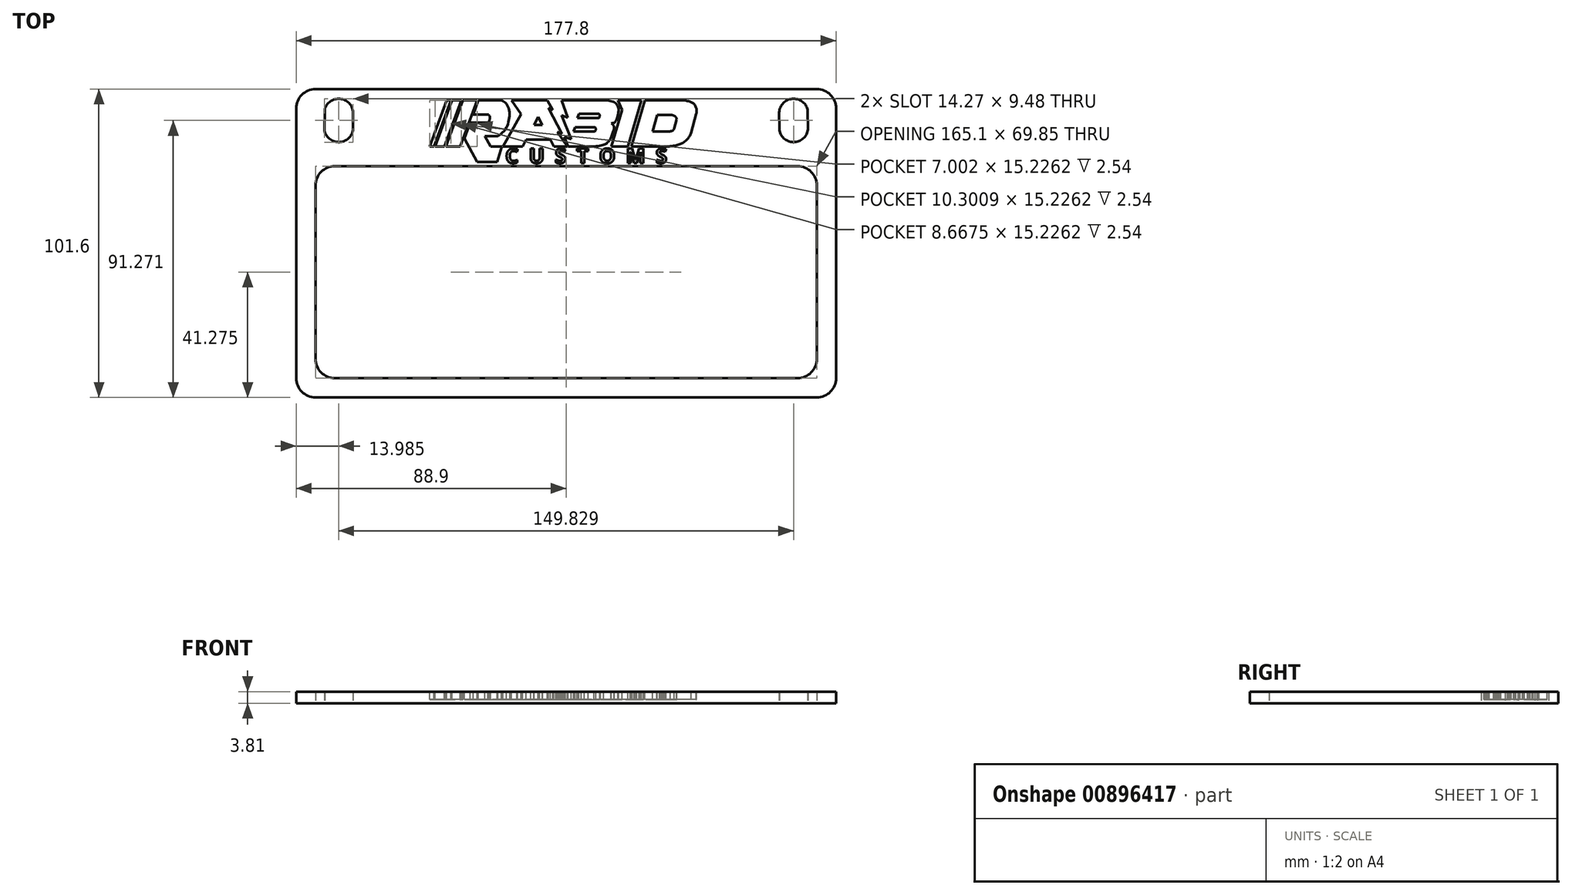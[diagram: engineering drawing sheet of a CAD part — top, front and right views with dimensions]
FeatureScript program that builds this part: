
annotation { "Feature Type Name" : "Feature", "Feature Type Description" : "" }
export const myFeature = defineFeature(function(context is Context, id is Id, definition is map)
    precondition{}
    {
        {
            var Q0;
            Q0=qCreatedBy(makeId("Top.planeOp"),FACE);
            var sketch = newSketch(context, id + "F0", { "sketchPlane" : qUnion([Q0])});
            skLineSegment(sketch, "E0.bottom", {"start": v(-82.55, 50.8) * mm, "end": v(82.55, 50.8) * mm});
            skLineSegment(sketch, "E0.top", {"start": v(-82.55, -50.8) * mm, "end": v(82.55, -50.8) * mm});
            skLineSegment(sketch, "E0.left", {"start": v(-88.9, 44.45) * mm, "end": v(-88.9, -44.45) * mm});
            skLineSegment(sketch, "E0.right", {"start": v(88.9, 44.45) * mm, "end": v(88.9, -44.45) * mm});
            skArc(sketch, "E1", {"start": v(-70.18, 43.14) * mm, "mid": v(-74.48, 47.6) * mm, "end": v(-79.55, 44.03) * mm});
            skArc(sketch, "E2", {"start": v(-79.65, 37.5) * mm, "mid": v(-74.85, 33.34) * mm, "end": v(-70.19, 37.65) * mm});
            skLineSegment(sketch, "E3", {"start": v(-79.55, 44.03) * mm, "end": v(-79.65, 37.5) * mm});
            skLineSegment(sketch, "E4", {"start": v(-70.18, 43.14) * mm, "end": v(-70.19, 37.65) * mm});
            skArc(sketch, "E5.filletArc", {"start": v(-82.55, 50.8) * mm, "mid": v(-87.04, 48.94) * mm, "end": v(-88.9, 44.45) * mm});
            skArc(sketch, "E6.filletArc", {"start": v(88.9, 44.45) * mm, "mid": v(87.04, 48.94) * mm, "end": v(82.55, 50.8) * mm});
            skArc(sketch, "E7.filletArc", {"start": v(82.55, -50.8) * mm, "mid": v(87.04, -48.94) * mm, "end": v(88.9, -44.45) * mm});
            skArc(sketch, "E8.filletArc", {"start": v(-88.9, -44.45) * mm, "mid": v(-87.04, -48.94) * mm, "end": v(-82.55, -50.8) * mm});
            skArc(sketch, "E9.MirrorCS", {"start": v(79.65, 37.5) * mm, "mid": v(74.85, 33.34) * mm, "end": v(70.19, 37.65) * mm});
            skLineSegment(sketch, "E10.MirrorCS", {"start": v(70.18, 43.14) * mm, "end": v(70.19, 37.65) * mm});
            skLineSegment(sketch, "E11.MirrorCS", {"start": v(79.55, 44.03) * mm, "end": v(79.65, 37.5) * mm});
            skArc(sketch, "E12.MirrorCS", {"start": v(70.18, 43.14) * mm, "mid": v(74.48, 47.6) * mm, "end": v(79.55, 44.03) * mm});
            skLineSegment(sketch, "E13.bottom", {"start": v(-76.2, 25.4) * mm, "end": v(76.2, 25.4) * mm});
            skLineSegment(sketch, "E13.top", {"start": v(-76.2, -44.45) * mm, "end": v(76.2, -44.45) * mm});
            skLineSegment(sketch, "E13.left", {"start": v(-82.55, 19.05) * mm, "end": v(-82.55, -38.1) * mm});
            skLineSegment(sketch, "E13.right", {"start": v(82.55, 19.05) * mm, "end": v(82.55, -38.1) * mm});
            skPoint(sketch, "E14.visualSharp", {"position": v(-82.55, 25.4) * mm});
            skArc(sketch, "E14.filletArc", {"start": v(-76.2, 25.4) * mm, "mid": v(-80.7, 23.54) * mm, "end": v(-82.55, 19.05) * mm});
            skPoint(sketch, "E15.visualSharp", {"position": v(82.55, 25.4) * mm});
            skArc(sketch, "E15.filletArc", {"start": v(82.55, 19.05) * mm, "mid": v(80.7, 23.54) * mm, "end": v(76.2, 25.4) * mm});
            skArc(sketch, "E16.filletArc", {"start": v(76.2, -44.45) * mm, "mid": v(80.7, -42.6) * mm, "end": v(82.55, -38.1) * mm});
            skArc(sketch, "E17.filletArc", {"start": v(-82.55, -38.1) * mm, "mid": v(-80.7, -42.6) * mm, "end": v(-76.2, -44.45) * mm});
            skSolve(sketch);
        }
        {
            var Q0;
            Q0=qSketchRegion(id+"F0",true);
            extrude(context, id + "F1", {"entities" : qUnion([Q0]), "depth" : 3.8 * mm, "offsetDistance" : 25.4 * mm});
        }
        {
            var Q0;
            Q0=makeQuery(id+"F1.opExtrude","CAP_FACE",FACE,{"disambiguationData":[OSD([sQuery(id+"F0.wireOp",EDGE,"E0.bottom"),sQuery(id+"F0.wireOp",EDGE,"E0.top"),sQuery(id+"F0.wireOp",EDGE,"E0.left"),sQuery(id+"F0.wireOp",EDGE,"E0.right"),sQuery(id+"F0.wireOp",EDGE,"5VO8HKmw-Esxs-SXYE-kqu2-tz63mqYEAXiB.bottom"),sQuery(id+"F0.wireOp",EDGE,"5VO8HKmw-Esxs-SXYE-kqu2-tz63mqYEAXiB.top"),sQuery(id+"F0.wireOp",EDGE,"5VO8HKmw-Esxs-SXYE-kqu2-tz63mqYEAXiB.left"),sQuery(id+"F0.wireOp",EDGE,"5VO8HKmw-Esxs-SXYE-kqu2-tz63mqYEAXiB.right"),sQuery(id+"F0.wireOp",EDGE,"ZtOqOz9P-OmnG-4Yyo-7eWy-nuA7kXPjKyah"),sQuery(id+"F0.wireOp",EDGE,"UhQ4hDFr-K4N2-AdQz-foQS-J1ex0guJvTy1"),sQuery(id+"F0.wireOp",EDGE,"N4FC6TI6-brI2-4AQh-qVUN-D9pu45Rl41Qv"),sQuery(id+"F0.wireOp",EDGE,"e420d8bd-9363-4734-b41a-eac7de9b64b6.trimOffspring"),sQuery(id+"F0.wireOp",EDGE,"E1"),sQuery(id+"F0.wireOp",EDGE,"E2"),sQuery(id+"F0.wireOp",EDGE,"E3"),sQuery(id+"F0.wireOp",EDGE,"E4"),sQuery(id+"F0.wireOp",EDGE,"388fb5a8-1ea3-4299-9213-5ed0e58871d10.MirrorCS"),sQuery(id+"F0.wireOp",EDGE,"388fb5a8-1ea3-4299-9213-5ed0e58871d11.MirrorCS"),sQuery(id+"F0.wireOp",EDGE,"388fb5a8-1ea3-4299-9213-5ed0e58871d12.MirrorCS"),sQuery(id+"F0.wireOp",EDGE,"388fb5a8-1ea3-4299-9213-5ed0e58871d13.MirrorCS"),sQuery(id+"F0.wireOp",EDGE,"388fb5a8-1ea3-4299-9213-5ed0e58871d14.MirrorCS"),sQuery(id+"F0.wireOp",EDGE,"388fb5a8-1ea3-4299-9213-5ed0e58871d15.MirrorCS"),sQuery(id+"F0.wireOp",EDGE,"388fb5a8-1ea3-4299-9213-5ed0e58871d16.MirrorCS"),sQuery(id+"F0.wireOp",EDGE,"e4d6ff06-b432-4113-9549-54836a44de97.trimOffspring"),sQuery(id+"F0.wireOp",EDGE,"343a162d-83e7-4e76-8459-f58917313968.filletArc"),sQuery(id+"F0.wireOp",EDGE,"E5.filletArc"),sQuery(id+"F0.wireOp",EDGE,"edaf4797-65b9-4c6f-aac9-da0511a8ee4a.filletArc"),sQuery(id+"F0.wireOp",EDGE,"E6.filletArc"),sQuery(id+"F0.wireOp",EDGE,"E7.filletArc"),sQuery(id+"F0.wireOp",EDGE,"03c890ec-8c51-4b18-90a4-88e655fb5f41.filletArc"),sQuery(id+"F0.wireOp",EDGE,"E8.filletArc"),sQuery(id+"F0.wireOp",EDGE,"408b96f7-1ce1-402e-bdab-98c03d327ea0.filletArc"),sQuery(id+"F0.wireOp",EDGE,"bjHKFNyx-CfJ5-pHdQ-Rjsu-5QMIBnfaj9aT"),sQuery(id+"F0.wireOp",EDGE,"hgvkDYSf-fWNe-M4NK-JL9C-AdpdUPqnzP5O"),sQuery(id+"F0.wireOp",EDGE,"OAJ1lY74-7GEf-kqh1-0pf5-185unJ51uZ2I"),sQuery(id+"F0.wireOp",EDGE,"7dc4cac3-4ac6-421c-a2db-e4ca0b0f0da1.trimOffspring"),sQuery(id+"F0.wireOp",EDGE,"83e6ecbc-63ed-4ffd-8922-6f6cd5348e8b.filletArc"),sQuery(id+"F0.wireOp",EDGE,"dcab3ff3-acb6-4ce3-92ec-6480daf3896c.filletArc"),sQuery(id+"F0.wireOp",EDGE,"7c8d1e97-1c9b-487b-8608-89f6ca3dd430.filletArc"),sQuery(id+"F0.wireOp",EDGE,"08c262f0-2f62-415d-b3e7-4e7392bdbc79.filletArc"),sQuery(id+"F0.wireOp",EDGE,"3e58efb5-ef9c-4a86-b57f-9bd11ee7677c.filletArc"),sQuery(id+"F0.wireOp",EDGE,"6554a4f9-b08c-4d9f-b403-859f83e8338b.filletArc"),sQuery(id+"F0.wireOp",EDGE,"495016f4-edd1-4ee5-bd80-bea4dd5b2a8f.filletArc"),sQuery(id+"F0.wireOp",EDGE,"2213c4b9-707a-4fd7-954b-32b890b75866.filletArc"),sQuery(id+"F0.wireOp",EDGE,"aa9dc5e7-3301-407e-8f38-505bf975b0c1.filletArc"),sQuery(id+"F0.wireOp",EDGE,"0aa655fa-f177-4ffa-a66b-476f03fc73f5.filletArc"),sQuery(id+"F0.wireOp",EDGE,"dca11e5c-dc25-4b1e-a035-025dcb39c10a.filletArc"),sQuery(id+"F0.wireOp",EDGE,"029dcba7-a7e0-4e25-897b-a3a4278317f0.filletArc")])],"isStart":false});
            var sketch = newSketch(context, id + "F2", { "sketchPlane" : qUnion([Q0])});
            skLineSegment(sketch, "E18", {"start": v(38.33, 47.13) * mm, "end": v(25.89, 47.13) * mm});
            skLineSegment(sketch, "E19", {"start": v(-44.97, 31.9) * mm, "end": v(-39.37, 47.13) * mm});
            skLineSegment(sketch, "E20", {"start": v(-34.91, 31.9) * mm, "end": v(-39.61, 31.9) * mm});
            skLineSegment(sketch, "E21", {"start": v(-37.97, 47.13) * mm, "end": v(-43.57, 31.9) * mm});
            skLineSegment(sketch, "E22", {"start": v(-43.14, 31.9) * mm, "end": v(-37.54, 47.13) * mm});
            skLineSegment(sketch, "E23", {"start": v(-34.47, 47.13) * mm, "end": v(-40.07, 31.9) * mm});
            skLineSegment(sketch, "E24", {"start": v(-39.61, 31.9) * mm, "end": v(-34, 47.13) * mm});
            skLineSegment(sketch, "E25", {"start": v(-29.31, 47.13) * mm, "end": v(-34.91, 31.9) * mm});
            skLineSegment(sketch, "E26", {"start": v(-30.63, 42.38) * mm, "end": v(-28.89, 47.13) * mm});
            skLineSegment(sketch, "E27", {"start": v(-30.63, 42.38) * mm, "end": v(-25.54, 42.38) * mm});
            skLineSegment(sketch, "E28", {"start": v(-25.82, 39.71) * mm, "end": v(-31.56, 39.71) * mm});
            skLineSegment(sketch, "E29", {"start": v(-31.56, 39.71) * mm, "end": v(-33.47, 34.53) * mm});
            skLineSegment(sketch, "E30", {"start": v(-33.47, 34.53) * mm, "end": v(-29.26, 26.81) * mm});
            skLineSegment(sketch, "E31", {"start": v(-29.26, 26.81) * mm, "end": v(-22.69, 26.81) * mm});
            skLineSegment(sketch, "E32", {"start": v(-22.69, 26.81) * mm, "end": v(-21.13, 31.94) * mm});
            skLineSegment(sketch, "E33", {"start": v(-21.13, 31.94) * mm, "end": v(-24.93, 31.94) * mm});
            skLineSegment(sketch, "E34", {"start": v(-24.93, 31.94) * mm, "end": v(-26.8, 35.36) * mm});
            skLineSegment(sketch, "E35", {"start": v(-26.8, 35.36) * mm, "end": v(-22.4, 35.36) * mm});
            skLineSegment(sketch, "E36", {"start": v(-20.82, 31.94) * mm, "end": v(-14.36, 31.94) * mm});
            skLineSegment(sketch, "E37", {"start": v(-17.99, 47.13) * mm, "end": v(-14.79, 42.6) * mm});
            skLineSegment(sketch, "E38", {"start": v(-14.79, 42.6) * mm, "end": v(-20.82, 31.94) * mm});
            skLineSegment(sketch, "E39", {"start": v(-14.36, 31.94) * mm, "end": v(-13.13, 34.12) * mm});
            skLineSegment(sketch, "E40", {"start": v(-13.13, 34.12) * mm, "end": v(-5.18, 34.12) * mm});
            skLineSegment(sketch, "E41", {"start": v(-5.18, 34.12) * mm, "end": v(-4.09, 31.94) * mm});
            skLineSegment(sketch, "E42", {"start": v(-6.16, 47.13) * mm, "end": v(-4.37, 44) * mm});
            skLineSegment(sketch, "E43", {"start": v(-4.37, 44) * mm, "end": v(-5.81, 44.53) * mm});
            skLineSegment(sketch, "E44", {"start": v(-5.81, 44.53) * mm, "end": v(-1.33, 36.07) * mm});
            skLineSegment(sketch, "E45", {"start": v(-1.33, 36.07) * mm, "end": v(-2.92, 36.65) * mm});
            skLineSegment(sketch, "E46", {"start": v(-2.92, 36.65) * mm, "end": v(0.37, 31.94) * mm});
            skLineSegment(sketch, "E47", {"start": v(-7.8, 39) * mm, "end": v(-10.55, 39) * mm});
            skLineSegment(sketch, "E48", {"start": v(-10.55, 39) * mm, "end": v(-9.25, 41.6) * mm});
            skLineSegment(sketch, "E49", {"start": v(-9.25, 41.6) * mm, "end": v(-7.8, 39) * mm});
            skLineSegment(sketch, "E50", {"start": v(-1.49, 47.13) * mm, "end": v(0.59, 41.43) * mm});
            skLineSegment(sketch, "E51", {"start": v(0.59, 41.43) * mm, "end": v(-1.5, 42.22) * mm});
            skLineSegment(sketch, "E52", {"start": v(-1.5, 42.22) * mm, "end": v(1.64, 34.27) * mm});
            skLineSegment(sketch, "E53", {"start": v(1.64, 34.27) * mm, "end": v(-0.57, 35.06) * mm});
            skLineSegment(sketch, "E54", {"start": v(-0.57, 35.06) * mm, "end": v(0.62, 31.94) * mm});
            skLineSegment(sketch, "E55", {"start": v(4.16, 42.63) * mm, "end": v(3.75, 41.22) * mm});
            skLineSegment(sketch, "E56", {"start": v(2.47, 36.82) * mm, "end": v(9.18, 36.82) * mm});
            skLineSegment(sketch, "E57", {"start": v(2.9, 38.29) * mm, "end": v(9.34, 38.29) * mm});
            skLineSegment(sketch, "E58", {"start": v(4.16, 42.63) * mm, "end": v(10.71, 42.63) * mm});
            skLineSegment(sketch, "E59", {"start": v(3.75, 41.22) * mm, "end": v(10.55, 41.22) * mm});
            skLineSegment(sketch, "E60", {"start": v(17, 47.13) * mm, "end": v(18.42, 43.92) * mm});
            skLineSegment(sketch, "E61", {"start": v(18.42, 43.92) * mm, "end": v(14.95, 31.94) * mm});
            skLineSegment(sketch, "E62", {"start": v(24.74, 47.13) * mm, "end": v(20.4, 31.94) * mm});
            skLineSegment(sketch, "E63", {"start": v(25.89, 47.13) * mm, "end": v(21.54, 31.94) * mm});
            skLineSegment(sketch, "E64", {"start": v(34.88, 42.24) * mm, "end": v(29.95, 42.24) * mm});
            skLineSegment(sketch, "E65", {"start": v(29.95, 42.24) * mm, "end": v(28.42, 36.88) * mm});
            skLineSegment(sketch, "E66", {"start": v(28.42, 36.88) * mm, "end": v(34.27, 36.88) * mm});
            skLineSegment(sketch, "E67", {"start": v(36.4, 40.65) * mm, "end": v(35.61, 37.9) * mm});
            skFitSpline(sketch, "E68", {"points": [v(42.85, 42.66) * mm, v(42.85, 44.51) * mm, v(42.05, 46) * mm, v(40.91, 46.64) * mm, v(38.33, 47.13) * mm], "startDerivative": vector(0.92, 7.51) * mm, "endDerivative": vector(-9.78, 0) * mm});
            skLineSegment(sketch, "E69", {"start": v(42.85, 42.66) * mm, "end": v(41.18, 36.43) * mm});
            skFitSpline(sketch, "E70", {"points": [v(14.89, 39.54) * mm, v(15.75, 39.73) * mm, v(16.34, 40.33) * mm, v(17.3, 43.6) * mm, v(17.07, 45.12) * mm, v(16.41, 46.04) * mm, v(15.07, 46.78) * mm, v(12.98, 47.13) * mm], "startDerivative": vector(8.08, 1.37) * mm, "endDerivative": vector(-11.23, 0) * mm});
            skFitSpline(sketch, "E71", {"points": [v(14.89, 39.54) * mm, v(15.43, 39.1) * mm, v(15.77, 38.31) * mm, v(15.72, 37.55) * mm, v(14.56, 34.34) * mm, v(13.66, 33.24) * mm, v(12.61, 32.53) * mm, v(11.32, 32.2) * mm, v(9.4, 31.94) * mm], "startDerivative": vector(6.57, -4.03) * mm, "endDerivative": vector(-13.6, 0) * mm});
            skFitSpline(sketch, "E72", {"points": [v(10.71, 42.63) * mm, v(10.88, 42.55) * mm, v(11, 42.33) * mm, v(10.93, 41.5) * mm, v(10.84, 41.32) * mm, v(10.55, 41.22) * mm], "startDerivative": vector(1.23, 0) * mm, "endDerivative": vector(-1.8, 0) * mm});
            skFitSpline(sketch, "E73", {"points": [v(9.34, 38.29) * mm, v(9.55, 38.2) * mm, v(9.7, 37.94) * mm, v(9.71, 37.22) * mm, v(9.58, 36.97) * mm, v(9.18, 36.82) * mm], "startDerivative": vector(1.5, 0) * mm, "endDerivative": vector(-3.48, -0.35) * mm});
            skFitSpline(sketch, "E74", {"points": [v(-21.27, 47.13) * mm, v(-20.13, 46.43) * mm, v(-19.27, 45.23) * mm, v(-18.66, 43.19) * mm, v(-18.78, 41) * mm, v(-19.44, 38.65) * mm, v(-20.73, 36.73) * mm, v(-22.4, 35.36) * mm], "startDerivative": vector(10.38, -5.2) * mm, "endDerivative": vector(-11.71, -8.5) * mm});
            skFitSpline(sketch, "E75", {"points": [v(34.88, 42.24) * mm, v(35.42, 42.11) * mm, v(35.84, 41.86) * mm, v(36.18, 41.49) * mm, v(36.4, 40.65) * mm], "startDerivative": vector(2.23, 0) * mm, "endDerivative": vector(-0.53, -4.33) * mm});
            skFitSpline(sketch, "E76", {"points": [v(34.27, 36.88) * mm, v(34.75, 37) * mm, v(35.18, 37.17) * mm, v(35.46, 37.5) * mm, v(35.61, 37.9) * mm], "startDerivative": vector(1.83, 0.4) * mm, "endDerivative": vector(0.53, 1.7) * mm});
            skLineSegment(sketch, "E77.trimOffspring", {"start": v(-37.97, 47.13) * mm, "end": v(-39.37, 47.13) * mm});
            skLineSegment(sketch, "E78.trimOffspring", {"start": v(-34.47, 47.13) * mm, "end": v(-37.54, 47.13) * mm});
            skLineSegment(sketch, "E79.trimOffspring", {"start": v(-29.31, 47.13) * mm, "end": v(-34, 47.13) * mm});
            skLineSegment(sketch, "E80.trimOffspring", {"start": v(-21.27, 47.13) * mm, "end": v(-28.89, 47.13) * mm});
            skLineSegment(sketch, "E81.trimOffspring", {"start": v(-40.07, 31.9) * mm, "end": v(-43.14, 31.9) * mm});
            skLineSegment(sketch, "E82.trimOffspring", {"start": v(-43.57, 31.9) * mm, "end": v(-44.97, 31.9) * mm});
            skLineSegment(sketch, "E83.trimOffspring", {"start": v(-4.09, 31.94) * mm, "end": v(0.37, 31.94) * mm});
            skLineSegment(sketch, "E84.trimOffspring", {"start": v(0.62, 31.94) * mm, "end": v(9.4, 31.94) * mm});
            skLineSegment(sketch, "E85.trimOffspring", {"start": v(-6.16, 47.13) * mm, "end": v(-17.99, 47.13) * mm});
            skLineSegment(sketch, "E86.trimOffspring", {"start": v(2.9, 38.29) * mm, "end": v(2.47, 36.82) * mm});
            skLineSegment(sketch, "E87.trimOffspring", {"start": v(12.98, 47.13) * mm, "end": v(-1.49, 47.13) * mm});
            skLineSegment(sketch, "E88.trimOffspring", {"start": v(14.95, 31.94) * mm, "end": v(20.4, 31.94) * mm});
            skLineSegment(sketch, "E89.trimOffspring", {"start": v(21.54, 31.94) * mm, "end": v(33.87, 31.94) * mm});
            skLineSegment(sketch, "E90.trimOffspring", {"start": v(24.74, 47.13) * mm, "end": v(17, 47.13) * mm});
            skFitSpline(sketch, "E91", {"points": [v(41.18, 36.43) * mm, v(40.7, 35.38) * mm, v(39.92, 34.28) * mm, v(38.78, 33.33) * mm, v(37.55, 32.67) * mm, v(36.09, 32.25) * mm, v(33.87, 31.94) * mm], "startDerivative": vector(-2.99, -7.22) * mm, "endDerivative": vector(-11.56, 0) * mm});
            skFitSpline(sketch, "E92", {"points": [v(-25.54, 42.38) * mm, v(-25.13, 41.77) * mm, v(-25.15, 40.9) * mm, v(-25.54, 39.98) * mm, v(-25.82, 39.71) * mm], "startDerivative": vector(2, -2.27) * mm, "endDerivative": vector(-1.51, -1.11) * mm});
            skText(sketch, "E93", { "text": "C  U  S  T  O  M  S", "fontName": "OpenSans-Bold.ttf"});
            const initialGuessF2  = {"E93": [-0.02, 0.0264, 1, 0, 0.00483]};
            skSetInitialGuess(sketch, initialGuessF2);
            skSolve(sketch);
        }
        {
            var Q0;
            Q0=qSketchRegion(id+"F2",true);
            extrude(context, id + "F3", {"entities" : qUnion([Q0]), "operationType" : NewBodyOperationType.REMOVE, "oppositeDirection" : true, "depth" : 2.54 * mm, "offsetDistance" : 25.4 * mm});
        }
    });
